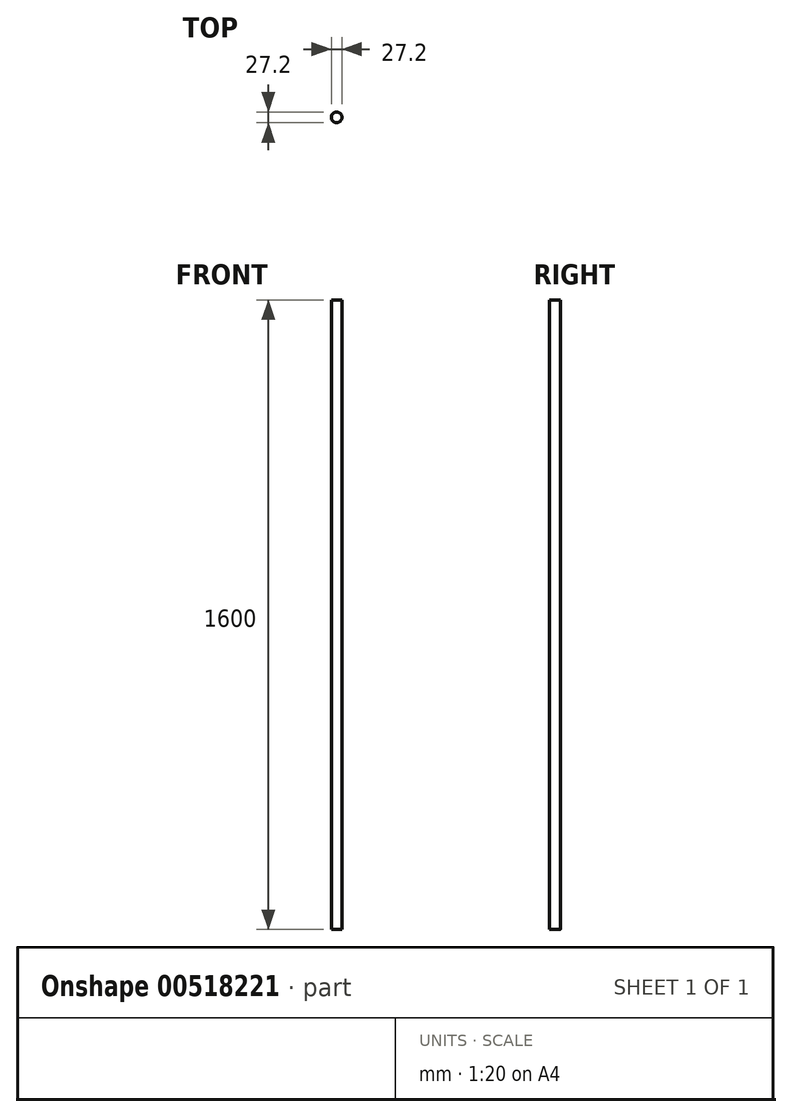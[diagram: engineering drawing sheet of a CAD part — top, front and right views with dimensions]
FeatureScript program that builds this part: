
annotation { "Feature Type Name" : "Feature", "Feature Type Description" : "" }
export const myFeature = defineFeature(function(context is Context, id is Id, definition is map)
    precondition{}
    {
        {
            var Q0;
            Q0=qCreatedBy(makeId("Top.planeOp"),FACE);
            var sketch = newSketch(context, id + "F0", { "sketchPlane" : qUnion([Q0])});
            skCircle(sketch, "E0", {"center": v(0, 0) * mm, "radius": 13.6 * mm});
            skSolve(sketch);
        }
        {
            var Q0;
            Q0=qSketchRegion(id+"F0",true);
            extrude(context, id + "F1", {"entities" : qUnion([Q0]), "depth" : 1600 * mm, "offsetDistance" : 25 * mm});
        }
    });
